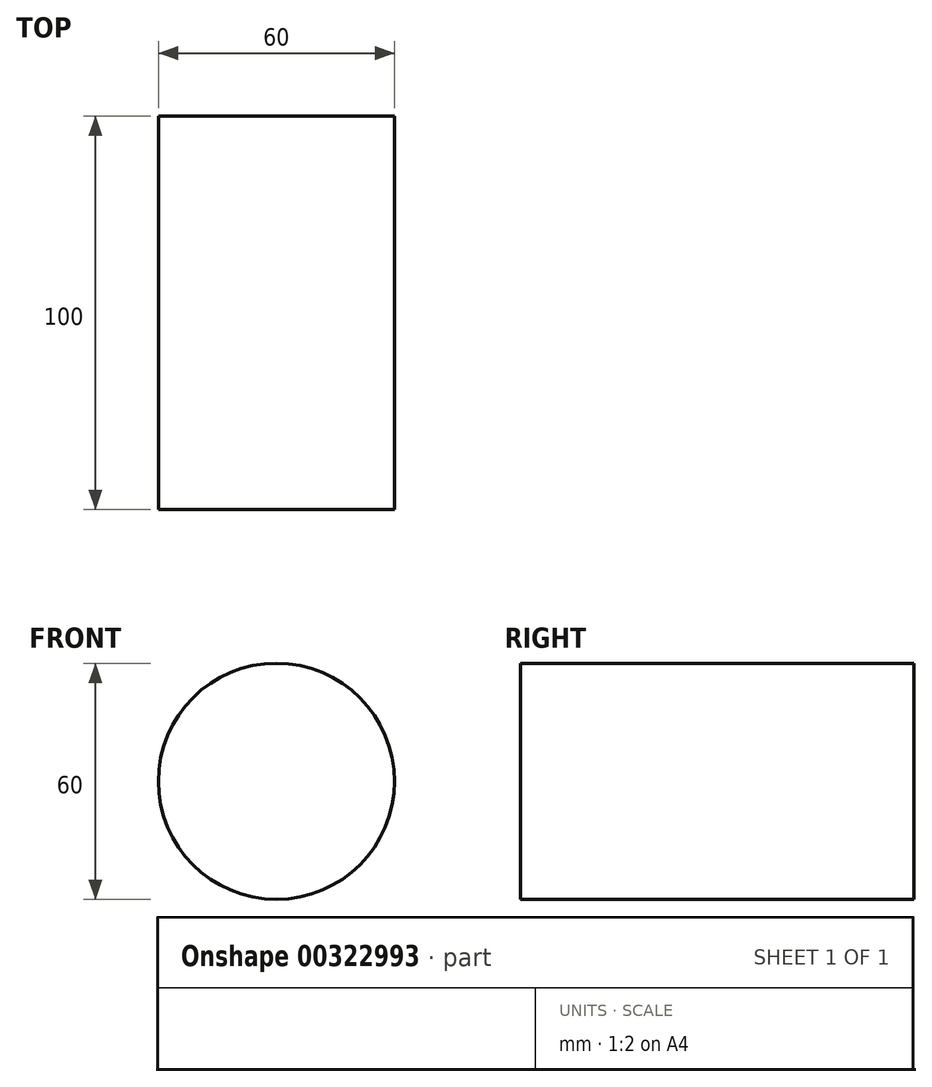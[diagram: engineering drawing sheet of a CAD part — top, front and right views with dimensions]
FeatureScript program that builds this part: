
annotation { "Feature Type Name" : "Feature", "Feature Type Description" : "" }
export const myFeature = defineFeature(function(context is Context, id is Id, definition is map)
    precondition{}
    {
        {
            var Q0;
            Q0=qCreatedBy(makeId("Front.planeOp"),FACE);
            var sketch = newSketch(context, id + "F0", { "sketchPlane" : qUnion([Q0])});
            skCircle(sketch, "E0", {"center": v(0, 0) * mm, "radius": 30 * mm});
            skSolve(sketch);
        }
        {
            var Q0;
            Q0=qSketchRegion(id+"F0",true);
            extrude(context, id + "F1", {"entities" : qUnion([Q0]), "depth" : 100 * mm, "symmetric" : true});
        }
    });
